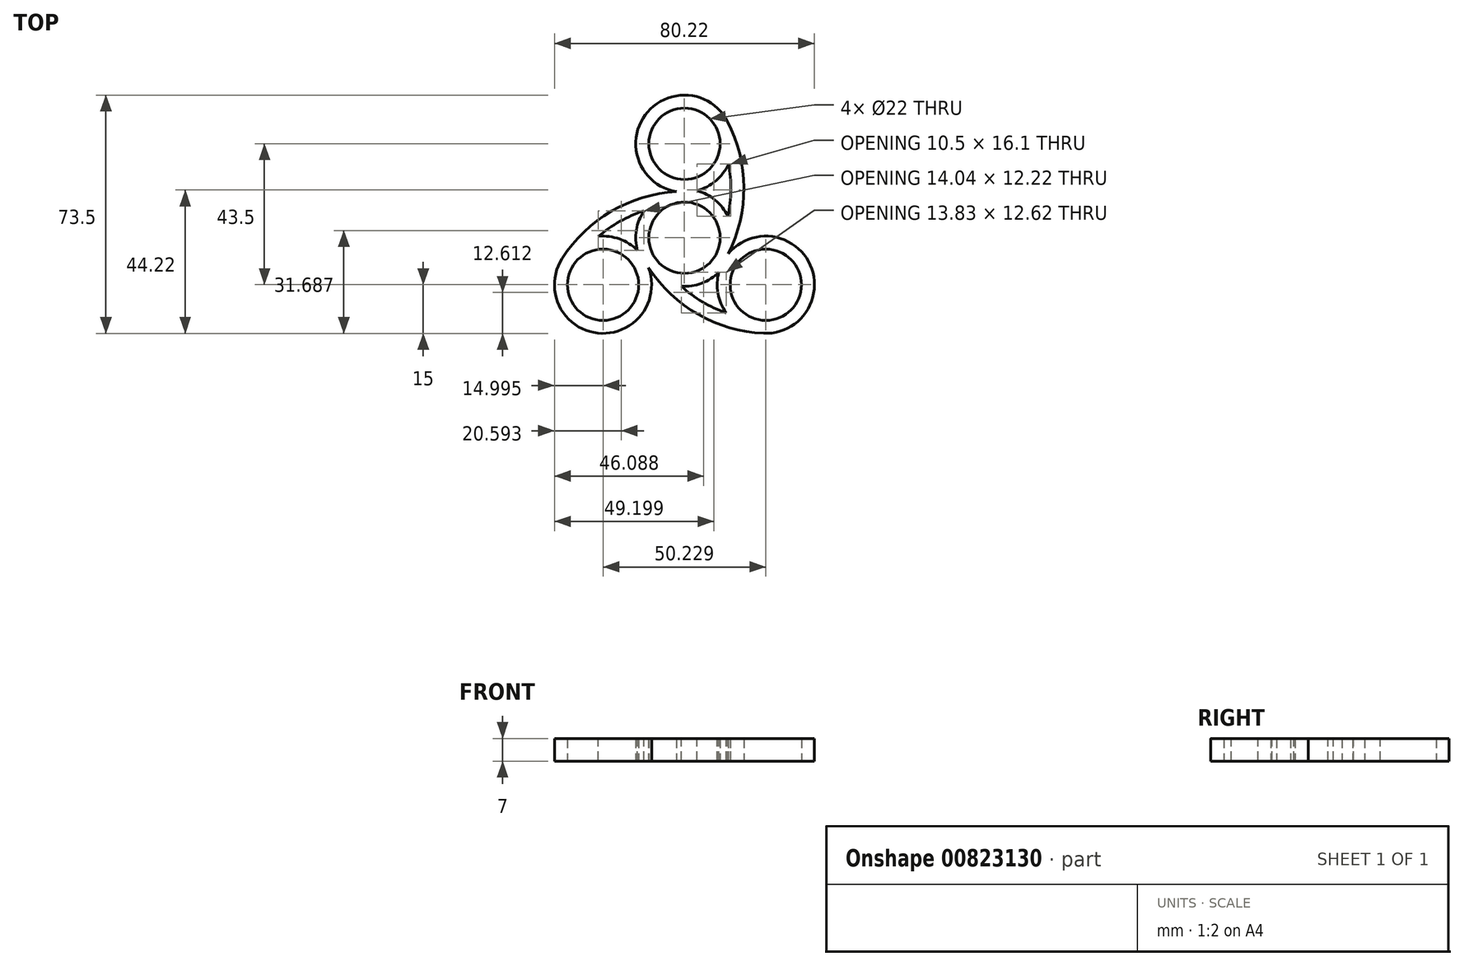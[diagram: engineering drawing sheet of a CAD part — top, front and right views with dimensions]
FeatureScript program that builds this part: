
annotation { "Feature Type Name" : "Feature", "Feature Type Description" : "" }
export const myFeature = defineFeature(function(context is Context, id is Id, definition is map)
    precondition{}
    {
        {
            var Q0;
            Q0=qCreatedBy(makeId("Top.planeOp"),FACE);
            var sketch = newSketch(context, id + "F0", { "sketchPlane" : qUnion([Q0])});
            skCircle(sketch, "E0", {"center": v(0, 0) * mm, "radius": 11 * mm});
            skCircle(sketch, "E1", {"center": v(0, 0) * mm, "radius": 43 * mm, "construction": true});
            skLineSegment(sketch, "E2", {"start": v(0, 0) * mm, "end": v(0, 43) * mm, "construction": true});
            skLineSegment(sketch, "E3", {"start": v(0, 0) * mm, "end": v(-37.24, -21.5) * mm, "construction": true});
            skLineSegment(sketch, "E4", {"start": v(0, 0) * mm, "end": v(37.24, -21.5) * mm, "construction": true});
            skCircle(sketch, "E5", {"center": v(0, 29) * mm, "radius": 11 * mm});
            skCircle(sketch, "E6", {"center": v(25.11, -14.5) * mm, "radius": 11 * mm});
            skCircle(sketch, "E7", {"center": v(-25.11, -14.5) * mm, "radius": 11 * mm});
            skCircle(sketch, "E8", {"center": v(0, 0) * mm, "radius": 29 * mm, "construction": true});
            skArc(sketch, "E9", {"start": v(-2.52, 14.21) * mm, "mid": v(-22.6, 8.13) * mm, "end": v(-37.74, -6.4) * mm});
            skArc(sketch, "E10", {"start": v(-37.74, -6.4) * mm, "mid": v(-26.73, -29.41) * mm, "end": v(-11.05, -9.29) * mm});
            skArc(sketch, "E11", {"start": v(-11.05, -9.29) * mm, "mid": v(4.26, -23.63) * mm, "end": v(24.4, -29.48) * mm});
            skArc(sketch, "E12", {"start": v(24.4, -29.48) * mm, "mid": v(38.84, -8.44) * mm, "end": v(13.57, -4.93) * mm});
            skArc(sketch, "E13", {"start": v(13.57, -4.93) * mm, "mid": v(18.34, 15.5) * mm, "end": v(13.33, 35.88) * mm});
            skArc(sketch, "E14", {"start": v(13.33, 35.88) * mm, "mid": v(-12.1, 37.86) * mm, "end": v(-2.52, 14.21) * mm});
            skLineSegment(sketch, "E15", {"start": v(-2.52, 14.21) * mm, "end": v(13.57, -4.93) * mm, "construction": true});
            skLineSegment(sketch, "E16", {"start": v(13.57, -4.93) * mm, "end": v(-11.05, -9.29) * mm, "construction": true});
            skLineSegment(sketch, "E17", {"start": v(-11.05, -9.29) * mm, "end": v(-2.52, 14.21) * mm, "construction": true});
            skSolve(sketch);
        }
        {
            var Q0;
            Q0 = qSketchRegion(id + "F0", true);
            extrude(context, id + "F1", {"entities" : qUnion([Q0]), "depth" : 7 * mm, "offsetDistance" : 25 * mm});
        }
        {
            var Q0;
            Q0=makeQuery(id+"F1.opExtrude","CAP_FACE",FACE,{"disambiguationData":[OSD([sQuery(id+"F0.wireOp",EDGE,"E0"),sQuery(id+"F0.wireOp",EDGE,"E5"),sQuery(id+"F0.wireOp",EDGE,"E6"),sQuery(id+"F0.wireOp",EDGE,"E7"),sQuery(id+"F0.wireOp",EDGE,"E9"),sQuery(id+"F0.wireOp",EDGE,"E10"),sQuery(id+"F0.wireOp",EDGE,"E11"),sQuery(id+"F0.wireOp",EDGE,"E12"),sQuery(id+"F0.wireOp",EDGE,"E13"),sQuery(id+"F0.wireOp",EDGE,"E14")])],"isStart":false});
            var sketch = newSketch(context, id + "F2", { "sketchPlane" : qUnion([Q0])});
            skArc(sketch, "E18", {"start": v(3.84, 14.5) * mm, "mid": v(9.67, 17.53) * mm, "end": v(13.64, 22.77) * mm});
            skArc(sketch, "E19", {"start": v(13.43, 6.67) * mm, "mid": v(14.34, 14.7) * mm, "end": v(13.64, 22.77) * mm});
            skArc(sketch, "E20", {"start": v(13.43, 6.67) * mm, "mid": v(9.48, 11.62) * mm, "end": v(3.84, 14.5) * mm});
            skLineSegment(sketch, "E21", {"start": v(9.67, 17.53) * mm, "end": v(0, 29) * mm, "construction": true});
            skLineSegment(sketch, "E22", {"start": v(9.48, 11.62) * mm, "end": v(0, 0) * mm, "construction": true});
            skArc(sketch, "E23.1.0", {"start": v(-12.5, 8.3) * mm, "mid": v(-14.8, 2.4) * mm, "end": v(-14.48, -3.92) * mm});
            skLineSegment(sketch, "E23.1.1", {"start": v(-20.02, -0.4) * mm, "end": v(-25.11, -14.5) * mm, "construction": true});
            skArc(sketch, "E23.1.2", {"start": v(-12.5, 8.3) * mm, "mid": v(-19.9, 5.06) * mm, "end": v(-26.54, 0.43) * mm});
            skArc(sketch, "E23.1.3", {"start": v(-14.48, -3.92) * mm, "mid": v(-20.02, -0.4) * mm, "end": v(-26.54, 0.43) * mm});
            skArc(sketch, "E23.2.0", {"start": v(-0.94, -14.97) * mm, "mid": v(5.32, -14.02) * mm, "end": v(10.64, -10.58) * mm});
            skLineSegment(sketch, "E23.2.1", {"start": v(10.35, -17.14) * mm, "end": v(25.11, -14.5) * mm, "construction": true});
            skArc(sketch, "E23.2.2", {"start": v(-0.94, -14.97) * mm, "mid": v(5.57, -19.77) * mm, "end": v(12.9, -23.2) * mm});
            skArc(sketch, "E23.2.3", {"start": v(10.64, -10.58) * mm, "mid": v(10.35, -17.14) * mm, "end": v(12.9, -23.2) * mm});
            skSolve(sketch);
        }
        {
            var Q0;
            Q0 = qSketchRegion(id + "F2", true);
            extrude(context, id + "F3", {"entities" : qUnion([Q0]), "operationType" : NewBodyOperationType.REMOVE, "oppositeDirection" : true, "depth" : 25 * mm, "offsetDistance" : 25 * mm});
        }
    });
